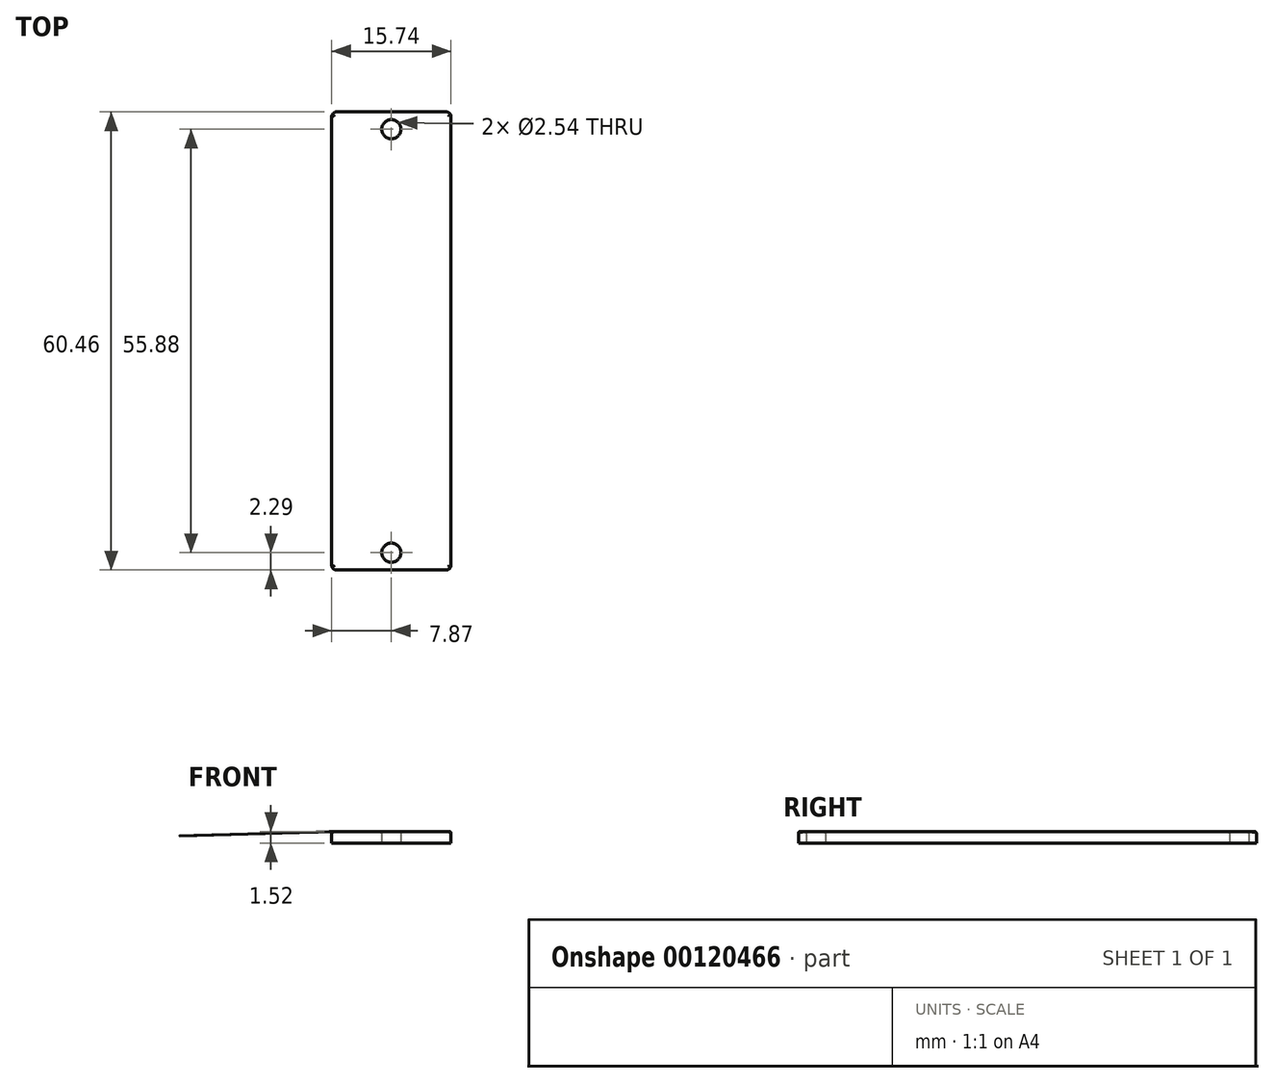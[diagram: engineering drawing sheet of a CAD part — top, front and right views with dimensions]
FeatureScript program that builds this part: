
annotation { "Feature Type Name" : "Feature", "Feature Type Description" : "" }
export const myFeature = defineFeature(function(context is Context, id is Id, definition is map)
    precondition{}
    {
        {
            var Q0;
            Q0=qCreatedBy(makeId("Top.planeOp"),FACE);
            var sketch = newSketch(context, id + "F0", { "sketchPlane" : qUnion([Q0])});
            skLineSegment(sketch, "E0.bottom", {"start": v(8, 30.48) * mm, "end": v(-8, 30.48) * mm});
            skLineSegment(sketch, "E0.top", {"start": v(8, -30.48) * mm, "end": v(-8, -30.48) * mm});
            skLineSegment(sketch, "E0.left", {"start": v(8, 30.48) * mm, "end": v(8, -30.48) * mm});
            skLineSegment(sketch, "E0.right", {"start": v(-8, 30.48) * mm, "end": v(-8, -30.48) * mm});
            skPoint(sketch, "E0.middle", {"position": v(0, 0) * mm});
            skCircle(sketch, "E1", {"center": v(0, 27.94) * mm, "radius": 1.27 * mm});
            skCircle(sketch, "E2", {"center": v(0, -27.94) * mm, "radius": 1.27 * mm});
            skLineSegment(sketch, "E3.bottom", {"start": v(9.9, 30.48) * mm, "end": v(-9.9, 30.48) * mm});
            skLineSegment(sketch, "E3.top", {"start": v(9.9, -30.48) * mm, "end": v(-9.9, -30.48) * mm});
            skLineSegment(sketch, "E3.left", {"start": v(9.9, 30.48) * mm, "end": v(9.9, -30.48) * mm});
            skLineSegment(sketch, "E3.right", {"start": v(-9.9, 30.48) * mm, "end": v(-9.9, -30.48) * mm});
            skSolve(sketch);
        }
        {
            var Q0;
            {var subQ2=sQuery(id+"F0.wireOp",EDGE,"E0.left");Q0=makeQuery(id+"F0.imprint","IMPRINT",FACE,{"disambiguationData":[TD([[makeQuery(id+"F0.imprint","IMPRINT",EDGE,{"derivedFrom":subQ2}),-1.0]])]});}
            var Q1;
            {var subQ0=sQuery(id+"F0.wireOp",EDGE,"E0.right");Q1=makeQuery(id+"F0.imprint","IMPRINT",FACE,{"disambiguationData":[TD([[makeQuery(id+"F0.imprint","IMPRINT",EDGE,{"derivedFrom":subQ0}),-1.0]])]});}
            var Q2;
            {var subQ0=sQuery(id+"F0.wireOp",EDGE,"E0.left");Q2=makeQuery(id+"F0.imprint","IMPRINT",FACE,{"disambiguationData":[TD([[makeQuery(id+"F0.imprint","IMPRINT",EDGE,{"derivedFrom":subQ0}),1.0]])]});}
            extrude(context, id + "F1", {"entities" : qUnion([Q0, Q1, Q2]), "depth" : 1.52 * mm});
        }
        {
            var Q0;
            Q0=makeQuery(id+"F1.opExtrude","CAP_EDGE",EDGE,{"disambiguationData":[OSD([sQuery(id+"F0.wireOp",EDGE,"E3.right")])],"isStart":false});
            var Q1;
            Q1=makeQuery(id+"F1.opExtrude","CAP_EDGE",EDGE,{"disambiguationData":[OSD([sQuery(id+"F0.wireOp",EDGE,"E3.left")])],"isStart":false});
            fillet(context, id + "F2", {"entities" : qUnion([Q0, Q1]), "radius" : 2.54 * mm, "tangentPropagation" : true, "allowEdgeOverflow" : false});
        }
        {
            var Q0;
            Q0=qCreatedBy(makeId("Top.planeOp"),FACE);
            var sketch = newSketch(context, id + "F3", { "sketchPlane" : qUnion([Q0])});
            skLineSegment(sketch, "E4.bottom", {"start": v(7.87, 30.48) * mm, "end": v(-7.87, 30.48) * mm});
            skLineSegment(sketch, "E4.top", {"start": v(7.87, -30.48) * mm, "end": v(-7.87, -30.48) * mm});
            skLineSegment(sketch, "E4.left", {"start": v(7.87, 30.48) * mm, "end": v(7.87, -30.48) * mm});
            skLineSegment(sketch, "E4.right", {"start": v(-7.87, 30.48) * mm, "end": v(-7.87, -30.48) * mm});
            skPoint(sketch, "E4.middle", {"position": v(0, 0) * mm});
            skLineSegment(sketch, "E5.bottom", {"start": v(11.62, 30.48) * mm, "end": v(-11.62, 30.48) * mm});
            skLineSegment(sketch, "E5.top", {"start": v(11.62, -30.48) * mm, "end": v(-11.62, -30.48) * mm});
            skLineSegment(sketch, "E5.left", {"start": v(11.62, 30.48) * mm, "end": v(11.62, -30.48) * mm});
            skLineSegment(sketch, "E5.right", {"start": v(-11.62, 30.48) * mm, "end": v(-11.62, -30.48) * mm});
            skLineSegment(sketch, "E6.bottom", {"start": v(7.87, 30.23) * mm, "end": v(-7.87, 30.23) * mm});
            skLineSegment(sketch, "E6.top", {"start": v(7.87, -30.23) * mm, "end": v(-7.87, -30.23) * mm});
            skLineSegment(sketch, "E6.left", {"start": v(7.87, 30.23) * mm, "end": v(7.87, -30.23) * mm});
            skLineSegment(sketch, "E6.right", {"start": v(-7.87, 30.23) * mm, "end": v(-7.87, -30.23) * mm});
            skSolve(sketch);
        }
        {
            var Q0;
            Q0 = qSketchRegion(id + "F3", true);
            extrude(context, id + "F4", {"entities" : qUnion([Q0]), "operationType" : NewBodyOperationType.REMOVE, "depth" : 25.4 * mm});
        }
        {
            var Q0;
            Q0=makeQuery(id+"F4.boolean.opBoolean","COPY",EDGE,{"derivedFrom":makeQuery(id+"F4.opExtrude","SWEPT_EDGE",EDGE,{"disambiguationData":[OSD([sQuery(id+"F3.wireOp",EDGE,"E4.right"),sQuery(id+"F3.wireOp",EDGE,"E6.bottom"),sQuery(id+"F3.wireOp",EDGE,"E6.right")])]})});
            var Q1;
            Q1=makeQuery(id+"F4.boolean.opBoolean","COPY",EDGE,{"derivedFrom":makeQuery(id+"F4.opExtrude","SWEPT_EDGE",EDGE,{"disambiguationData":[OSD([sQuery(id+"F3.wireOp",EDGE,"E4.left"),sQuery(id+"F3.wireOp",EDGE,"E6.bottom"),sQuery(id+"F3.wireOp",EDGE,"E6.left")])]})});
            var Q2;
            Q2=makeQuery(id+"F4.boolean.opBoolean","COPY",EDGE,{"derivedFrom":makeQuery(id+"F4.opExtrude","SWEPT_EDGE",EDGE,{"disambiguationData":[OSD([sQuery(id+"F3.wireOp",EDGE,"E4.right"),sQuery(id+"F3.wireOp",EDGE,"E6.top"),sQuery(id+"F3.wireOp",EDGE,"E6.right")])]})});
            var Q3;
            Q3=makeQuery(id+"F4.boolean.opBoolean","COPY",EDGE,{"derivedFrom":makeQuery(id+"F4.opExtrude","SWEPT_EDGE",EDGE,{"disambiguationData":[OSD([sQuery(id+"F3.wireOp",EDGE,"E4.left"),sQuery(id+"F3.wireOp",EDGE,"E6.top"),sQuery(id+"F3.wireOp",EDGE,"E6.left")])]})});
            var Q4;
            Q4=makeQuery(id+"F4.boolean.opBoolean","COPY",EDGE,{"derivedFrom":makeQuery(id+"F4.opExtrude","CAP_EDGE",EDGE,{"disambiguationData":[OSD([sQuery(id+"F3.wireOp",EDGE,"E6.top")])],"isStart":true})});
            var Q5;
            Q5=makeQuery(id+"F4.boolean.opBoolean","COPY",EDGE,{"derivedFrom":makeQuery(id+"F4.opExtrude","CAP_EDGE",EDGE,{"disambiguationData":[OSD([sQuery(id+"F3.wireOp",EDGE,"E6.right")])],"isStart":true})});
            var Q6;
            Q6=makeQuery(id+"F4.boolean.opBoolean","COPY",EDGE,{"derivedFrom":makeQuery(id+"F4.opExtrude","CAP_EDGE",EDGE,{"disambiguationData":[OSD([sQuery(id+"F3.wireOp",EDGE,"E6.bottom")])],"isStart":true})});
            var Q7;
            Q7=makeQuery(id+"F4.boolean.opBoolean","COPY",EDGE,{"derivedFrom":makeQuery(id+"F4.opExtrude","CAP_EDGE",EDGE,{"disambiguationData":[OSD([sQuery(id+"F3.wireOp",EDGE,"E6.left")])],"isStart":true})});
            fillet(context, id + "F5", {"entities" : qUnion([Q0, Q1, Q2, Q3, Q4, Q5, Q6, Q7]), "radius" : 0.64 * mm, "tangentPropagation" : true, "allowEdgeOverflow" : false});
        }
        {
            var Q0;
            Q0=makeQuery(id+"F4.boolean.opBoolean","INTERSECT",EDGE,{"derivedFrom":[makeQuery(id+"F1.opExtrude","CAP_FACE",FACE,{"disambiguationData":[OSD([sQuery(id+"F0.wireOp",EDGE,"E1"),sQuery(id+"F0.wireOp",EDGE,"E2"),sQuery(id+"F0.wireOp",EDGE,"E3.bottom"),sQuery(id+"F0.wireOp",EDGE,"E3.top"),sQuery(id+"F0.wireOp",EDGE,"E3.left"),sQuery(id+"F0.wireOp",EDGE,"E3.right")])],"isStart":false}),makeQuery(id+"F4.opExtrude","SWEPT_FACE",FACE,{"disambiguationData":[OSD([sQuery(id+"F3.wireOp",EDGE,"E6.top")])]})]});
            var Q1;
            Q1=makeQuery(id+"F1.opExtrude","CAP_EDGE",EDGE,{"disambiguationData":[OSD([sQuery(id+"F0.wireOp",EDGE,"E2")])],"isStart":false});
            var Q2;
            Q2=makeQuery(id+"F1.opExtrude","CAP_EDGE",EDGE,{"disambiguationData":[OSD([sQuery(id+"F0.wireOp",EDGE,"E1")])],"isStart":false});
            fillet(context, id + "F6", {"entities" : qUnion([Q0, Q1, Q2]), "radius" : 0.25 * mm, "tangentPropagation" : true, "allowEdgeOverflow" : false});
        }
    });
